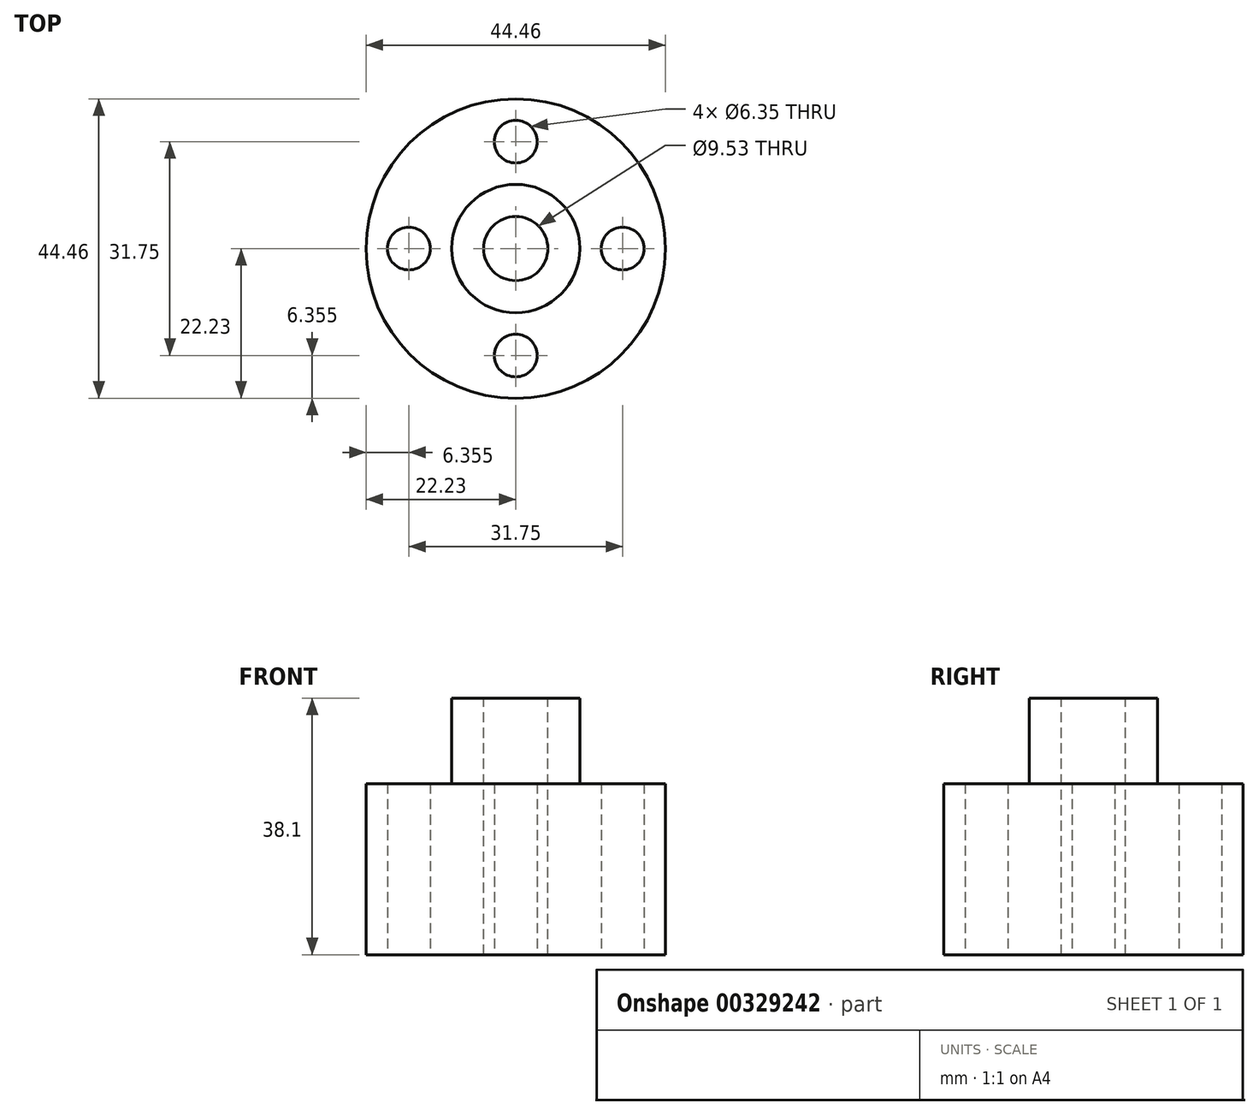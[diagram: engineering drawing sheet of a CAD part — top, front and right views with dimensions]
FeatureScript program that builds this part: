
annotation { "Feature Type Name" : "Feature", "Feature Type Description" : "" }
export const myFeature = defineFeature(function(context is Context, id is Id, definition is map)
    precondition{}
    {
        {
            var Q0;
            Q0=qCreatedBy(makeId("Top.planeOp"),FACE);
            var sketch = newSketch(context, id + "F0", { "sketchPlane" : qUnion([Q0])});
            skCircle(sketch, "E0", {"center": v(0, 0) * mm, "radius": 4.76 * mm});
            skCircle(sketch, "E1", {"center": v(0, 0) * mm, "radius": 9.53 * mm});
            skCircle(sketch, "E2", {"center": v(0, 0) * mm, "radius": 15.88 * mm});
            skCircle(sketch, "E3", {"center": v(0, 0) * mm, "radius": 22.23 * mm});
            skCircle(sketch, "E4", {"center": v(15.88, 0) * mm, "radius": 3.18 * mm});
            skCircle(sketch, "E5", {"center": v(0, 15.88) * mm, "radius": 3.18 * mm});
            skCircle(sketch, "E6", {"center": v(-15.88, 0) * mm, "radius": 3.18 * mm});
            skCircle(sketch, "E7", {"center": v(0, -15.88) * mm, "radius": 3.18 * mm});
            skSolve(sketch);
        }
        {
            var Q0;
            Q0=makeQuery(id+"F0.imprint","IMPRINT",FACE,{"disambiguationData":[TD([[makeQuery(id+"F0.imprint","IMPRINT",EDGE,{"derivedFrom":sQuery(id+"F0.wireOp",EDGE,"E3")}),1.0]])]});
            var Q1;
            Q1=makeQuery(id+"F0.imprint","IMPRINT",FACE,{"disambiguationData":[TD([[makeQuery(id+"F0.imprint","IMPRINT",EDGE,{"derivedFrom":sQuery(id+"F0.wireOp",EDGE,"E1")}),-1.0]])]});
            extrude(context, id + "F1", {"entities" : qUnion([Q0, Q1]), "depth" : 25.4 * mm});
        }
        {
            var Q0;
            Q0=makeQuery(id+"F0.imprint","IMPRINT",FACE,{"disambiguationData":[TD([[makeQuery(id+"F0.imprint","IMPRINT",EDGE,{"derivedFrom":sQuery(id+"F0.wireOp",EDGE,"E0")}),-1.0]])]});
            var Q1;
            Q1=makeQuery(id+"F0.imprint","IMPRINT",FACE,{"disambiguationData":[TD([[makeQuery(id+"F0.imprint","IMPRINT",EDGE,{"derivedFrom":sQuery(id+"F0.wireOp",EDGE,"E0")}),1.0]])]});
            extrude(context, id + "F2", {"entities" : qUnion([Q0, Q1]), "operationType" : NewBodyOperationType.ADD, "depth" : 38.1 * mm});
        }
        {
            var Q0;
            Q0=makeQuery(id+"F2.opExtrude","CAP_FACE",FACE,{"disambiguationData":[OSD([sQuery(id+"F0.wireOp",EDGE,"E1")])],"isStart":false});
            var sketch = newSketch(context, id + "F3", { "sketchPlane" : qUnion([Q0])});
            skCircle(sketch, "E8", {"center": v(0, 0) * mm, "radius": 4.76 * mm});
            skSolve(sketch);
        }
        {
            var Q0;
            Q0=makeQuery(id+"F3.imprint","IMPRINT",FACE,{"disambiguationData":[TD([[makeQuery(id+"F3.imprint","IMPRINT",EDGE,{"derivedFrom":sQuery(id+"F3.wireOp",EDGE,"E8")}),1.0]])]});
            extrude(context, id + "F4", {"entities" : qUnion([Q0]), "operationType" : NewBodyOperationType.REMOVE, "oppositeDirection" : true, "depth" : 38.1 * mm});
        }
    });
